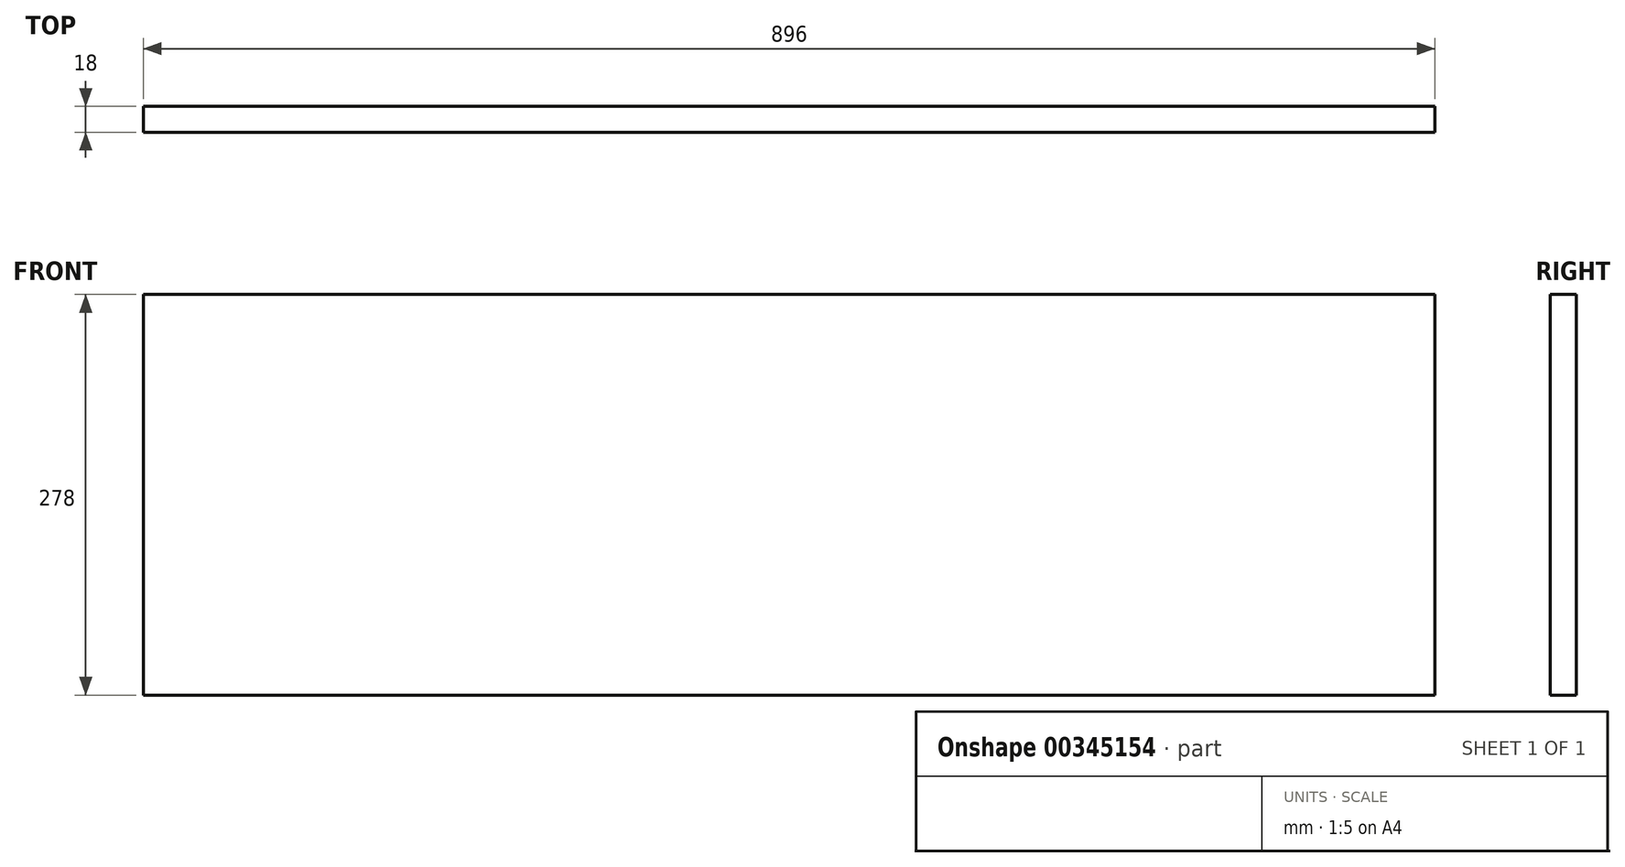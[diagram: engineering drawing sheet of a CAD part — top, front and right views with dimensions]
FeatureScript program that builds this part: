
annotation { "Feature Type Name" : "Feature", "Feature Type Description" : "" }
export const myFeature = defineFeature(function(context is Context, id is Id, definition is map)
    precondition{}
    {
        {
            var Q0;
            Q0=qCreatedBy(makeId("Front.planeOp"),FACE);
            var sketch = newSketch(context, id + "F0", { "sketchPlane" : qUnion([Q0])});
            skLineSegment(sketch, "E0.bottom", {"start": v(0, 0) * mm, "end": v(63.87, 0) * mm});
            skLineSegment(sketch, "E0.top", {"start": v(0, 55.2) * mm, "end": v(63.87, 55.2) * mm});
            skLineSegment(sketch, "E0.left", {"start": v(0, 0) * mm, "end": v(0, 55.2) * mm});
            skLineSegment(sketch, "E0.right", {"start": v(63.87, 0) * mm, "end": v(63.87, 55.2) * mm});
            skSolve(sketch);
        }
        {
            var Q0;
            Q0=makeQuery(id+"F0.imprint","IMPRINT",FACE,{"disambiguationData":[TD([[makeQuery(id+"F0.imprint","IMPRINT",EDGE,{"derivedFrom":sQuery(id+"F0.wireOp",EDGE,"E0.bottom")}),1.0]])]});
            extrude(context, id + "F1", {"entities" : qUnion([Q0]), "depth" : 18 * mm});
        }
        {
            var Q0;
            Q0=makeQuery(id+"F1.opExtrude","SWEPT_FACE",FACE,{"disambiguationData":[OSD([sQuery(id+"F0.wireOp",EDGE,"E0.left")])]});
            extrude(context, id + "F2", {"entities" : qUnion([Q0]), "operationType" : NewBodyOperationType.ADD, "oppositeDirection" : true, "depth" : 896 * mm});
        }
        {
            var Q0;
            {var subQ0=sQuery(id+"F0.wireOp",EDGE,"E0.bottom");Q0=makeQuery(id+"F2.boolean.opBoolean","MERGE",FACE,{"derivedFrom":[makeQuery(id+"F1.opExtrude","SWEPT_FACE",FACE,{"disambiguationData":[OSD([subQ0])]}),makeQuery(id+"F2.opExtrude","SWEPT_FACE",FACE,{"disambiguationData":[OSD([subQ0,sQuery(id+"F0.wireOp",EDGE,"E0.left")])]})]});}
            extrude(context, id + "F3", {"entities" : qUnion([Q0]), "operationType" : NewBodyOperationType.ADD, "oppositeDirection" : true, "depth" : 280 * mm});
        }
        {
            var Q0;
            {var subQ0=sQuery(id+"F0.wireOp",EDGE,"E0.bottom");Q0=makeQuery(id+"F2.boolean.opBoolean","MERGE",FACE,{"derivedFrom":[makeQuery(id+"F1.opExtrude","SWEPT_FACE",FACE,{"disambiguationData":[OSD([subQ0])]}),makeQuery(id+"F2.opExtrude","SWEPT_FACE",FACE,{"disambiguationData":[OSD([subQ0,sQuery(id+"F0.wireOp",EDGE,"E0.left")])]})]});}
            extrude(context, id + "F4", {"entities" : qUnion([Q0]), "operationType" : NewBodyOperationType.ADD, "oppositeDirection" : true, "depth" : 25 * mm});
        }
        {
            var Q0;
            Q0=makeQuery(id+"F3.opExtrude","CAP_FACE",FACE,{"disambiguationData":[OSD([sQuery(id+"F0.wireOp",EDGE,"E0.bottom"),sQuery(id+"F0.wireOp",EDGE,"E0.left")])],"isStart":false});
            extrude(context, id + "F5", {"entities" : qUnion([Q0]), "operationType" : NewBodyOperationType.REMOVE, "oppositeDirection" : true, "depth" : 2 * mm});
        }
    });
